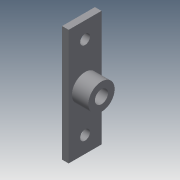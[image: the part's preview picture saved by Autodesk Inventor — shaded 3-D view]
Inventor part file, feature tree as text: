
AUTODESK INVENTOR PART (.ipt)
format: ipt  version: 2013 (Build 170138000, 138)  size: 97,792 bytes
history: native  units: mm
features: extrude x4, sketch x4
ambient origin geometry x8: Origin, YZ Plane, XZ Plane, XY Plane, X Axis, Y Axis, Z Axis, Center Point
bodies: Solid1 (feature_tree)
feature tree (8):
  extrude  "Extrusion1"  Depth=10.0mm
  extrude  "Extrusion2"  Depth=8.0mm
  extrude  "Extrusion3"  Depth=4.0mm
  extrude  "Extrusion4"  Depth=5.0mm
  sketch  "Sketch1"  dims[d0=35.186mm d2=10.0mm]
  sketch  "Sketch2"  dims[d3=2.0mm d4=0.0mm d5=8.0mm]
  sketch  "Sketch3"  dims[d6=5.0mm d7=0.0mm d8=4.0mm]
  sketch  "Sketch4"  dims[d9=7.0mm d10=0.0mm d11=5.0mm d12=5.0mm d13=3.0mm d14=3.0mm d15=2.0mm d16=0.0mm]
